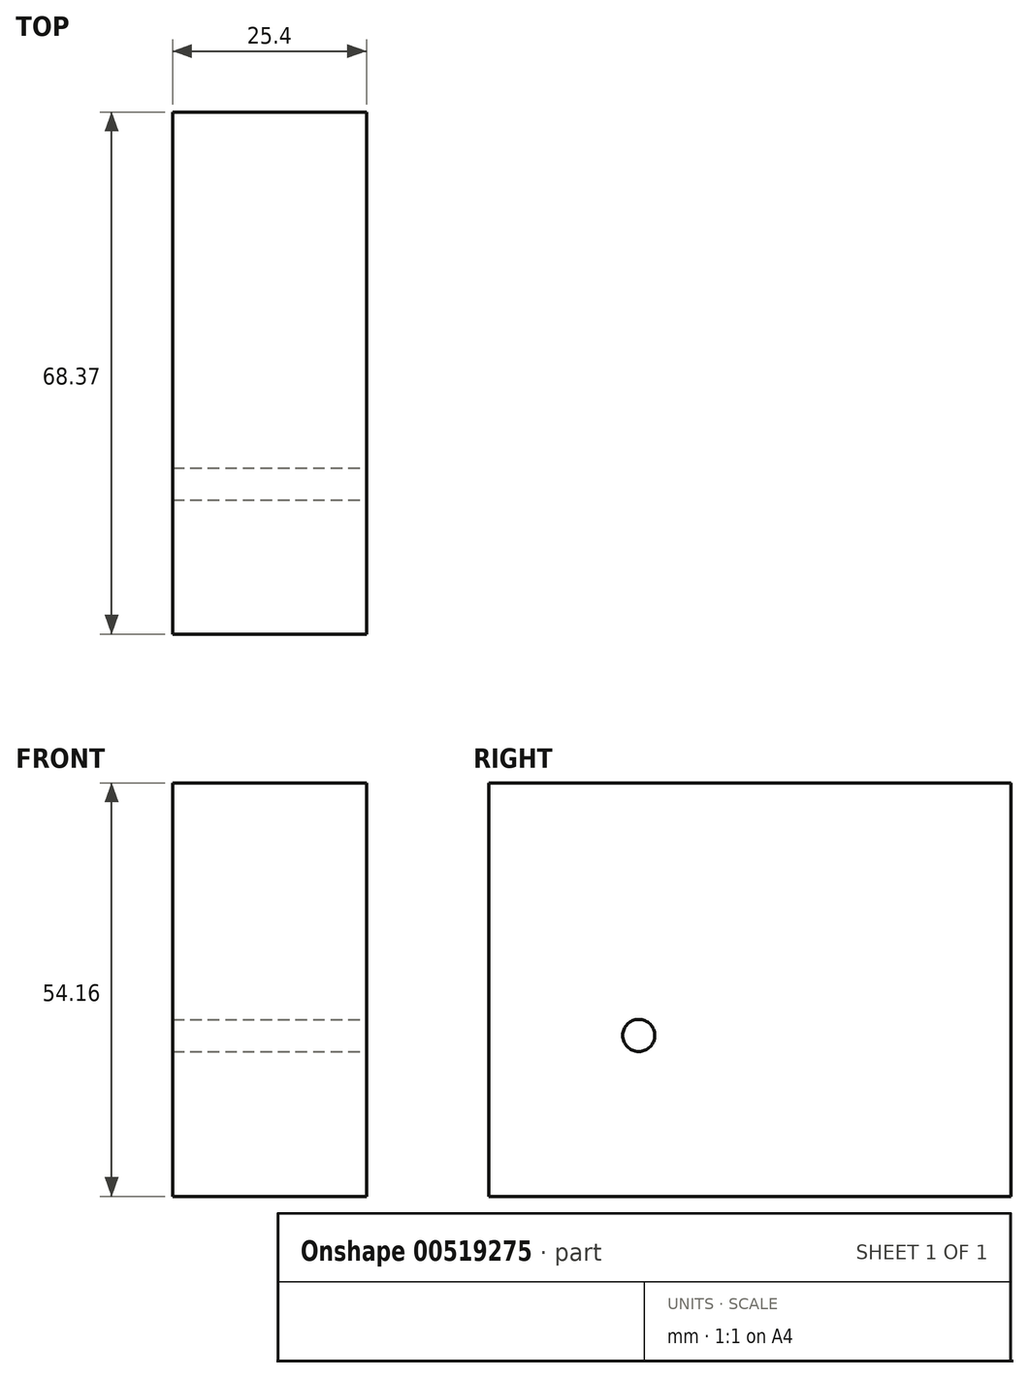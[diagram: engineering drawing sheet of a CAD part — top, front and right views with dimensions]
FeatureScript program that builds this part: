
annotation { "Feature Type Name" : "Feature", "Feature Type Description" : "" }
export const myFeature = defineFeature(function(context is Context, id is Id, definition is map)
    precondition{}
    {
        {
            var Q0;
            Q0=qCreatedBy(makeId("Right.planeOp"),FACE);
            var sketch = newSketch(context, id + "F0", { "sketchPlane" : qUnion([Q0])});
            skLineSegment(sketch, "E0.bottom", {"start": v(33.57, 27.08) * mm, "end": v(-34.8, 27.08) * mm});
            skLineSegment(sketch, "E0.top", {"start": v(33.57, -27.08) * mm, "end": v(-34.8, -27.08) * mm});
            skLineSegment(sketch, "E0.left", {"start": v(33.57, 27.08) * mm, "end": v(33.57, -27.08) * mm});
            skLineSegment(sketch, "E0.right", {"start": v(-34.8, 27.08) * mm, "end": v(-34.8, -27.08) * mm});
            skSolve(sketch);
        }
        {
            var Q0;
            Q0 = qSketchRegion(id + "F0", true);
            extrude(context, id + "F1", {"entities" : qUnion([Q0]), "depth" : 25.4 * mm, "offsetDistance" : 25.4 * mm});
        }
        {
            var Q0;
            Q0=makeQuery(id+"F1.opExtrude","CAP_FACE",FACE,{"disambiguationData":[OSD([sQuery(id+"F0.wireOp",EDGE,"E0.bottom"),sQuery(id+"F0.wireOp",EDGE,"E0.top"),sQuery(id+"F0.wireOp",EDGE,"E0.left"),sQuery(id+"F0.wireOp",EDGE,"E0.right")])],"isStart":false});
            var sketch = newSketch(context, id + "F2", { "sketchPlane" : qUnion([Q0])});
            skLineSegment(sketch, "E1", {"start": v(-15.16, -6) * mm, "end": v(10.38, -6) * mm});
            skSolve(sketch);
        }
        {
            var Q0;
            Q0=sQuery(id+"F2.wireOp",VERTEX,"E1.start");
            var Q1;
            Q1=makeQuery(id+"F1.opExtrude","SWEPT_BODY",BODY,{"disambiguationData":[OSD([sQuery(id+"F0.wireOp",EDGE,"E0.bottom"),sQuery(id+"F0.wireOp",EDGE,"E0.top"),sQuery(id+"F0.wireOp",EDGE,"E0.left"),sQuery(id+"F0.wireOp",EDGE,"E0.right")])]});
            hole(context, id + "F3", {"style" : HoleStyle.SIMPLE, "endStyle" : HoleEndStyle.THROUGH, "standardTappedOrClearance" : lookupTablePath({ "standard" : "ISO", "engagement" : "75%", "pitch" : "0.8 mm", "size" : "M5", "type" : "Tapped" }), "standardBlindInLast" : lookupTablePath({ "standard" : "ISO", "engagement" : "75%", "pitch" : "0.8 mm", "size" : "M5", "type" : "Tapped" }), "holeDiameter" : 4.2 * mm, "showTappedDepth" : true, "isTappedThrough" : true, "tappedDepth" : 12.7 * mm, "tapClearance" : 3, "locations" : qUnion([Q0]), "scope" : qUnion([Q1]), "majorDiameter" : 5 * mm});
        }
    });
